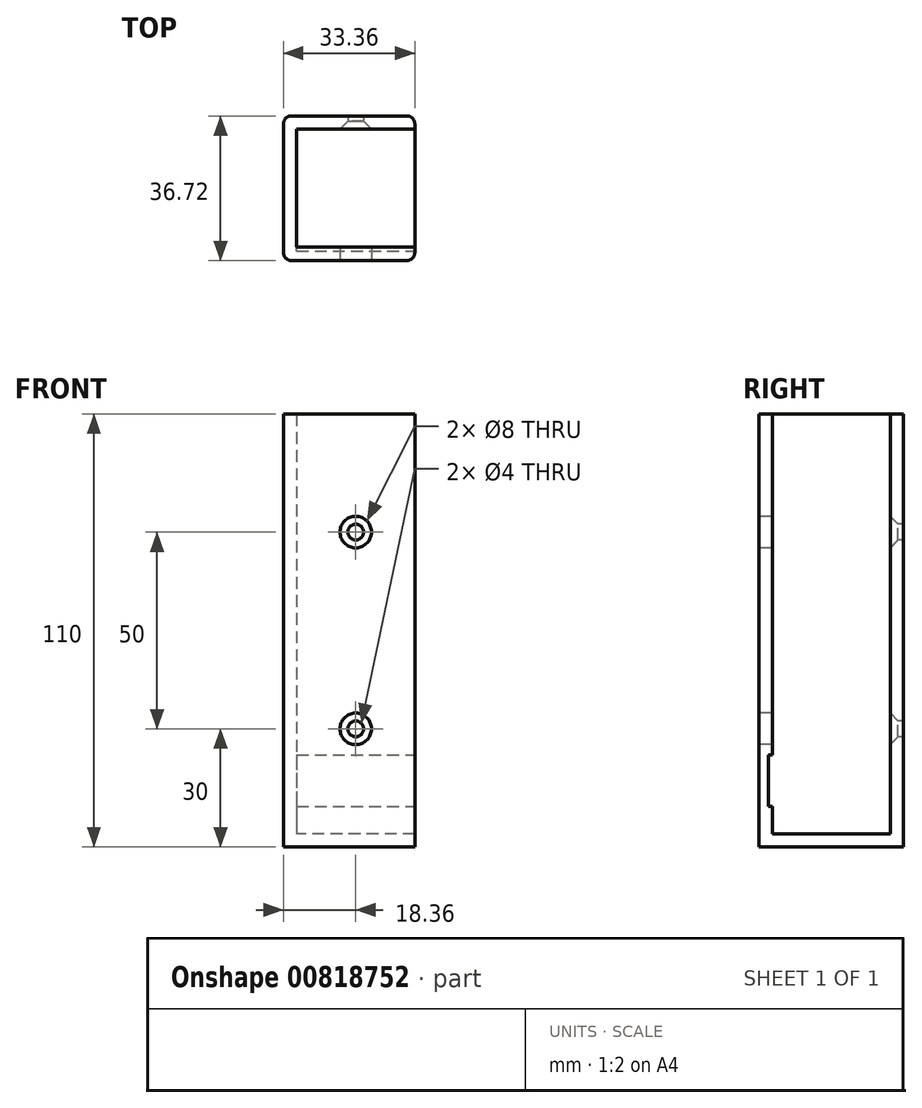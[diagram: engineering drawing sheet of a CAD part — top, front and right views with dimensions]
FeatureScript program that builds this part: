
annotation { "Feature Type Name" : "Feature", "Feature Type Description" : "" }
export const myFeature = defineFeature(function(context is Context, id is Id, definition is map)
    precondition{}
    {
        {
            var Q0;
            Q0=qCreatedBy(makeId("Top.planeOp"),FACE);
            var sketch = newSketch(context, id + "F0", { "sketchPlane" : qUnion([Q0])});
            skLineSegment(sketch, "E0.bottom", {"start": v(15, -15) * mm, "end": v(-15, -15) * mm});
            skLineSegment(sketch, "E0.top", {"start": v(15, 15) * mm, "end": v(-15, 15) * mm});
            skLineSegment(sketch, "E0.left", {"start": v(15, -15) * mm, "end": v(15, 15) * mm});
            skLineSegment(sketch, "E0.right", {"start": v(-15, -15) * mm, "end": v(-15, 15) * mm});
            skPoint(sketch, "E0.middle", {"position": v(0, 0) * mm});
            skLineSegment(sketch, "E1", {"start": v(15, 15) * mm, "end": v(15, 18.36) * mm});
            skLineSegment(sketch, "E2", {"start": v(-18.36, 18.36) * mm, "end": v(15, 18.36) * mm});
            skLineSegment(sketch, "E3", {"start": v(15, 0) * mm, "end": v(-15, 0) * mm, "construction": true});
            skLineSegment(sketch, "E4.MirrorCS", {"start": v(-18.36, -18.36) * mm, "end": v(15, -18.36) * mm});
            skLineSegment(sketch, "E5", {"start": v(15, -15) * mm, "end": v(15, -18.36) * mm});
            skLineSegment(sketch, "E6", {"start": v(-18.36, 18.36) * mm, "end": v(-18.36, -18.36) * mm});
            skSolve(sketch);
        }
        {
            var Q0;
            Q0=makeQuery(id+"F0.imprint","IMPRINT",FACE,{"disambiguationData":[TD([[makeQuery(id+"F0.imprint","IMPRINT",EDGE,{"derivedFrom":sQuery(id+"F0.wireOp",EDGE,"E0.bottom")}),1.0]])]});
            extrude(context, id + "F1", {"entities" : qUnion([Q0]), "depth" : 110 * mm, "offsetDistance" : 25 * mm});
        }
        {
            var Q0;
            Q0=makeQuery(id+"F0.imprint","IMPRINT",FACE,{"disambiguationData":[TD([[makeQuery(id+"F0.imprint","IMPRINT",EDGE,{"derivedFrom":sQuery(id+"F0.wireOp",EDGE,"E0.bottom")}),-1.0]])]});
            extrude(context, id + "F2", {"entities" : qUnion([Q0]), "operationType" : NewBodyOperationType.ADD, "depth" : 3.36 * mm, "offsetDistance" : 25 * mm});
        }
        {
            var Q0;
            Q0=makeQuery(id+"F1.opExtrude","SWEPT_EDGE",EDGE,{"disambiguationData":[OSD([sQuery(id+"F0.wireOp",EDGE,"E4.MirrorCS"),sQuery(id+"F0.wireOp",EDGE,"E6")])]});
            var Q1;
            Q1=makeQuery(id+"F1.opExtrude","SWEPT_EDGE",EDGE,{"disambiguationData":[OSD([sQuery(id+"F0.wireOp",EDGE,"E2"),sQuery(id+"F0.wireOp",EDGE,"E6")])]});
            var Q2;
            Q2=makeQuery(id+"F1.opExtrude","SWEPT_EDGE",EDGE,{"disambiguationData":[OSD([sQuery(id+"F0.wireOp",EDGE,"E4.MirrorCS"),sQuery(id+"F0.wireOp",EDGE,"E5")])]});
            var Q3;
            Q3=makeQuery(id+"F1.opExtrude","SWEPT_EDGE",EDGE,{"disambiguationData":[OSD([sQuery(id+"F0.wireOp",EDGE,"E1"),sQuery(id+"F0.wireOp",EDGE,"E2")])]});
            fillet(context, id + "F3", {"entities" : qUnion([Q0, Q1, Q2, Q3]), "radius" : 2 * mm, "tangentPropagation" : true, "allowEdgeOverflow" : false});
        }
        {
            var Q0;
            Q0=makeQuery(id+"F1.opExtrude","SWEPT_FACE",FACE,{"disambiguationData":[OSD([sQuery(id+"F0.wireOp",EDGE,"E4.MirrorCS")])]});
            var sketch = newSketch(context, id + "F4", { "sketchPlane" : qUnion([Q0])});
            skPoint(sketch, "E7", {"position": v(0, 30) * mm});
            skPoint(sketch, "E8", {"position": v(0, 80) * mm});
            skSolve(sketch);
        }
        {
            var Q0;
            Q0=sQuery(id+"F4.wireOp",VERTEX,"E7");
            var Q1;
            Q1=sQuery(id+"F4.wireOp",VERTEX,"E8");
            var Q2;
            Q2=makeQuery(id+"F1.opExtrude","SWEPT_BODY",BODY,{"disambiguationData":[OSD([sQuery(id+"F0.wireOp",EDGE,"E0.bottom"),sQuery(id+"F0.wireOp",EDGE,"E0.top"),sQuery(id+"F0.wireOp",EDGE,"E0.right"),sQuery(id+"F0.wireOp",EDGE,"E1"),sQuery(id+"F0.wireOp",EDGE,"E2"),sQuery(id+"F0.wireOp",EDGE,"E4.MirrorCS"),sQuery(id+"F0.wireOp",EDGE,"E5"),sQuery(id+"F0.wireOp",EDGE,"E6")])]});
            hole(context, id + "F5", {"style" : HoleStyle.SIMPLE, "endStyle" : HoleEndStyle.BLIND, "holeDiameter" : 8 * mm, "majorDiameter" : 5 * mm, "holeDepth" : 4 * mm, "isTappedThrough" : true, "tappedDepth" : 12 * mm, "tapClearance" : 3, "startFromSketch" : true, "locations" : qUnion([Q0, Q1]), "scope" : qUnion([Q2])});
        }
        {
            var Q0;
            Q0=makeQuery(id+"F1.opExtrude","SWEPT_FACE",FACE,{"disambiguationData":[OSD([sQuery(id+"F0.wireOp",EDGE,"E0.top")])]});
            var sketch = newSketch(context, id + "F6", { "sketchPlane" : qUnion([Q0])});
            skPoint(sketch, "E9", {"position": v(0, 30) * mm});
            skLineSegment(sketch, "E10", {"start": v(15, 56.68) * mm, "end": v(-15, 56.68) * mm, "construction": true});
            skPoint(sketch, "E11", {"position": v(0, 80) * mm});
            skPoint(sketch, "E11.positionSnap0", {"position": v(0, 56.68) * mm});
            skSolve(sketch);
        }
        {
            var Q0;
            Q0=sQuery(id+"F6.wireOp",VERTEX,"E9");
            var Q1;
            Q1=sQuery(id+"F6.wireOp",VERTEX,"E11");
            var Q2;
            Q2=makeQuery(id+"F1.opExtrude","SWEPT_BODY",BODY,{"disambiguationData":[OSD([sQuery(id+"F0.wireOp",EDGE,"E0.bottom"),sQuery(id+"F0.wireOp",EDGE,"E0.top"),sQuery(id+"F0.wireOp",EDGE,"E0.right"),sQuery(id+"F0.wireOp",EDGE,"E1"),sQuery(id+"F0.wireOp",EDGE,"E2"),sQuery(id+"F0.wireOp",EDGE,"E4.MirrorCS"),sQuery(id+"F0.wireOp",EDGE,"E5"),sQuery(id+"F0.wireOp",EDGE,"E6")])]});
            hole(context, id + "F7", {"style" : HoleStyle.C_SINK, "endStyle" : HoleEndStyle.BLIND, "holeDiameter" : 4 * mm, "cSinkDiameter" : 8 * mm, "cSinkAngle" : 90 * degree, "majorDiameter" : 5 * mm, "holeDepth" : 4 * mm, "isTappedThrough" : true, "tappedDepth" : 12 * mm, "tapClearance" : 3, "startFromSketch" : true, "locations" : qUnion([Q0, Q1]), "scope" : qUnion([Q2])});
        }
        {
            var Q0;
            Q0=makeQuery(id+"F1.opExtrude","SWEPT_FACE",FACE,{"disambiguationData":[OSD([sQuery(id+"F0.wireOp",EDGE,"E0.bottom")])]});
            var sketch = newSketch(context, id + "F8", { "sketchPlane" : qUnion([Q0])});
            skLineSegment(sketch, "E12.bottom", {"start": v(15, 3.36) * mm, "end": v(-15, 3.36) * mm, "construction": true});
            skLineSegment(sketch, "E12.top", {"start": v(15, 10.36) * mm, "end": v(-15, 10.36) * mm, "construction": true});
            skLineSegment(sketch, "E12.left", {"start": v(15, 3.36) * mm, "end": v(15, 10.36) * mm, "construction": true});
            skLineSegment(sketch, "E12.right", {"start": v(-15, 3.36) * mm, "end": v(-15, 10.36) * mm, "construction": true});
            skLineSegment(sketch, "E13.bottom", {"start": v(15, 10.36) * mm, "end": v(-15, 10.36) * mm});
            skLineSegment(sketch, "E13.top", {"start": v(15, 23.36) * mm, "end": v(-15, 23.36) * mm});
            skLineSegment(sketch, "E13.left", {"start": v(15, 10.36) * mm, "end": v(15, 23.36) * mm});
            skLineSegment(sketch, "E13.right", {"start": v(-15, 10.36) * mm, "end": v(-15, 23.36) * mm});
            skSolve(sketch);
        }
        {
            var Q0;
            Q0=makeQuery(id+"F8.imprint","IMPRINT",FACE,{"disambiguationData":[TD([[makeQuery(id+"F8.imprint","IMPRINT",EDGE,{"derivedFrom":sQuery(id+"F8.wireOp",EDGE,"E13.bottom")}),-1.0]])]});
            extrude(context, id + "F9", {"entities" : qUnion([Q0]), "operationType" : NewBodyOperationType.REMOVE, "oppositeDirection" : true, "depth" : 1 * mm, "offsetDistance" : 25 * mm});
        }
    });
